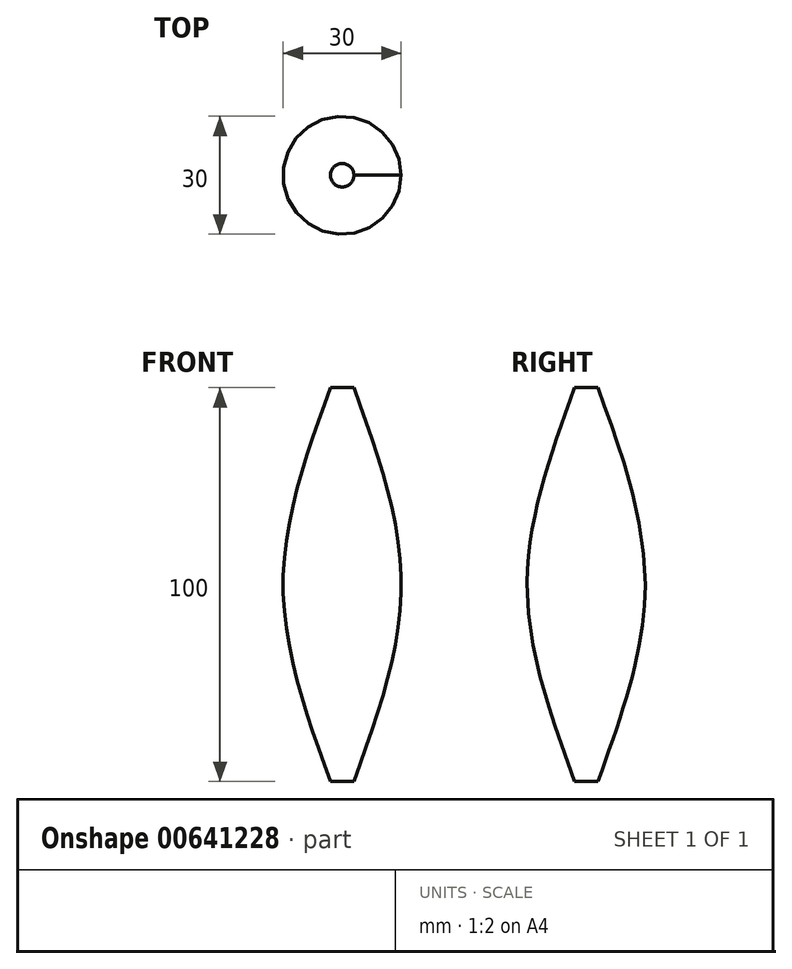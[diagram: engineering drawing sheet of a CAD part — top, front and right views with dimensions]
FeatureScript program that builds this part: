
annotation { "Feature Type Name" : "Feature", "Feature Type Description" : "" }
export const myFeature = defineFeature(function(context is Context, id is Id, definition is map)
    precondition{}
    {
        {
            var Q0;
            Q0=qCreatedBy(makeId("Top.planeOp"),FACE);
            var sketch = newSketch(context, id + "F0", { "sketchPlane" : qUnion([Q0])});
            skCircle(sketch, "E0", {"center": v(0, 0) * mm, "radius": 3 * mm});
            skSolve(sketch);
        }
        {
            var Q0;
            Q0=qCreatedBy(makeId("Top.planeOp"),FACE);
            cPlane(context, id + "F1", {"entities" : qUnion([Q0]), "cplaneType" : CPlaneType.OFFSET, "offset" : 100 * mm, "width" : 150 * mm, "height" : 150 * mm});
        }
        {
            var Q0;
            Q0=qCreatedBy(id+"F1.planeOp",FACE);
            var sketch = newSketch(context, id + "F2", { "sketchPlane" : qUnion([Q0])});
            skCircle(sketch, "E1.0", {"center": v(0, 0) * mm, "radius": 3 * mm});
            skSolve(sketch);
        }
        {
            var Q0;
            Q0=qCreatedBy(makeId("Top.planeOp"),FACE);
            cPlane(context, id + "F3", {"entities" : qUnion([Q0]), "cplaneType" : CPlaneType.OFFSET, "offset" : 50 * mm, "width" : 150 * mm, "height" : 150 * mm});
        }
        {
            var Q0;
            Q0=qCreatedBy(id+"F3.planeOp",FACE);
            var sketch = newSketch(context, id + "F4", { "sketchPlane" : qUnion([Q0])});
            skCircle(sketch, "E2", {"center": v(0, 0) * mm, "radius": 15 * mm});
            skSolve(sketch);
        }
        {
            var Q0;
            Q0 = qSketchRegion(id + "F0", true);
            var Q1;
            Q1 = qSketchRegion(id + "F4", true);
            var Q2;
            Q2 = qSketchRegion(id + "F2", true);
            loft(context, id + "F5", {"sheetProfilesArray" : [{ "sheetProfileEntities" : qUnion([Q0]) }, { "sheetProfileEntities" : qUnion([Q1]) }, { "sheetProfileEntities" : qUnion([Q2]) }]});
        }
    });
